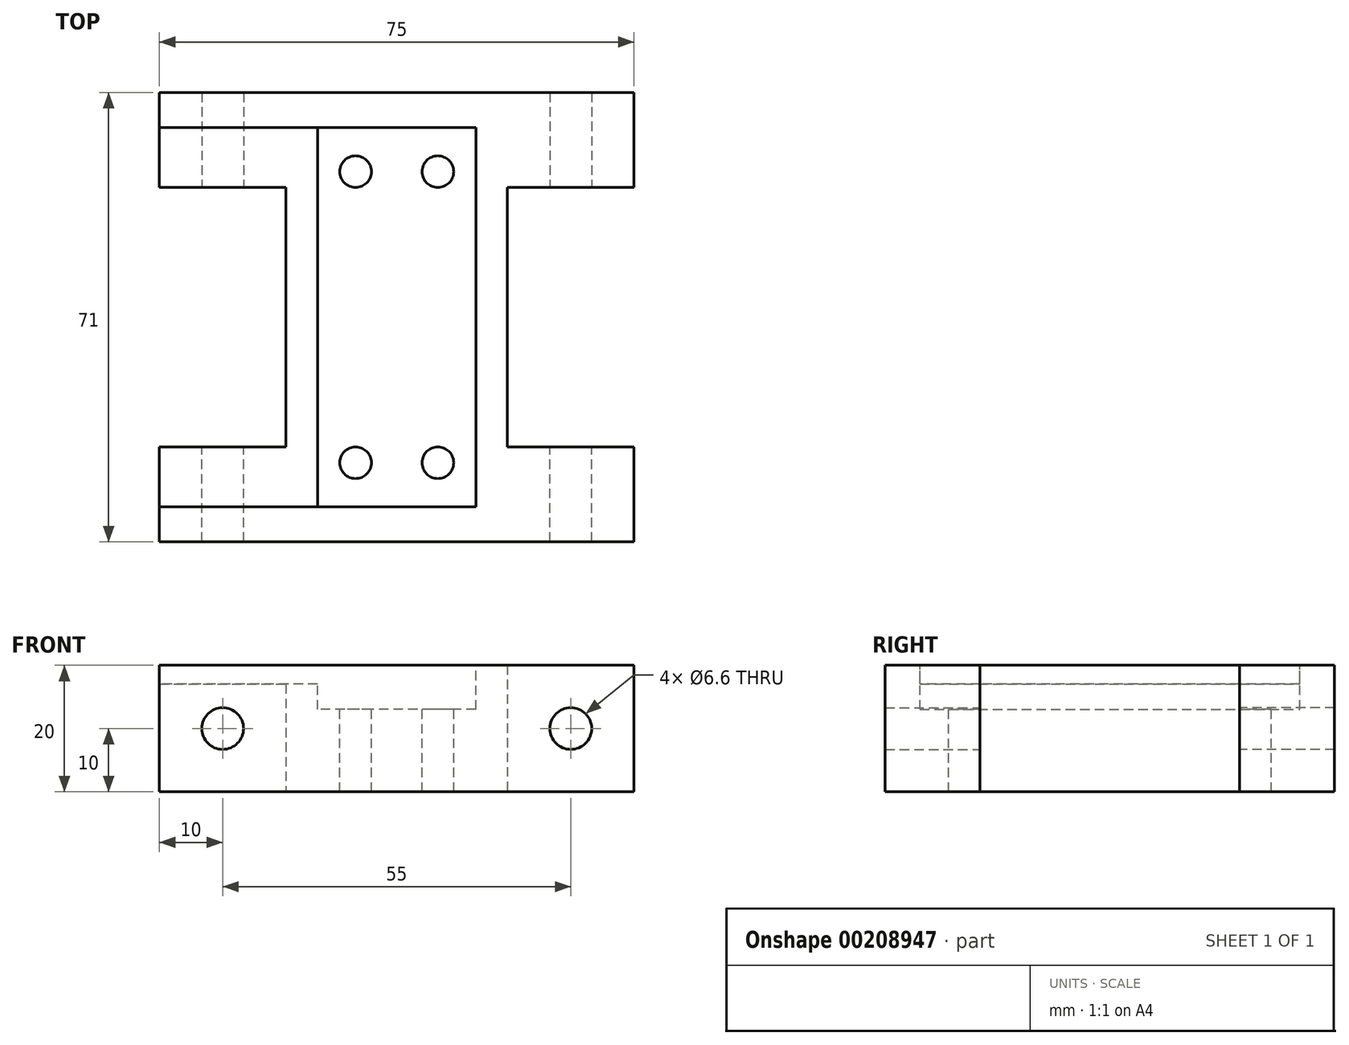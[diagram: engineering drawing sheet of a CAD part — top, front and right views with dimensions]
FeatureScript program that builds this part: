
annotation { "Feature Type Name" : "Feature", "Feature Type Description" : "" }
export const myFeature = defineFeature(function(context is Context, id is Id, definition is map)
    precondition{}
    {
        {
            var Q0;
            Q0=qCreatedBy(makeId("Top.planeOp"),FACE);
            var sketch = newSketch(context, id + "F0", { "sketchPlane" : qUnion([Q0])});
            skLineSegment(sketch, "E0.bottom", {"start": v(-37.5, 35.5) * mm, "end": v(37.5, 35.5) * mm});
            skLineSegment(sketch, "E0.top", {"start": v(-37.5, -35.5) * mm, "end": v(37.5, -35.5) * mm});
            skLineSegment(sketch, "E0.left", {"start": v(-37.5, 35.5) * mm, "end": v(-37.5, 20.5) * mm});
            skLineSegment(sketch, "E0.right", {"start": v(37.5, 35.5) * mm, "end": v(37.5, 20.5) * mm});
            skLineSegment(sketch, "E1", {"start": v(-37.5, 0) * mm, "end": v(37.5, 0) * mm, "construction": true});
            skPoint(sketch, "E1.endSnap0", {"position": v(37.5, 0) * mm});
            skLineSegment(sketch, "E2", {"start": v(0, 35.5) * mm, "end": v(0, -35.5) * mm, "construction": true});
            skLineSegment(sketch, "E3", {"start": v(-37.5, 20.5) * mm, "end": v(-17.5, 20.5) * mm});
            skLineSegment(sketch, "E4", {"start": v(-17.5, 20.5) * mm, "end": v(-17.5, 0) * mm});
            skLineSegment(sketch, "E5.MirrorCS", {"start": v(17.5, 20.5) * mm, "end": v(17.5, 0) * mm});
            skLineSegment(sketch, "E6.MirrorCS", {"start": v(37.5, 20.5) * mm, "end": v(17.5, 20.5) * mm});
            skLineSegment(sketch, "E7.MirrorCS", {"start": v(-17.5, -20.5) * mm, "end": v(-17.5, 0) * mm});
            skLineSegment(sketch, "E8.MirrorCS", {"start": v(17.5, -20.5) * mm, "end": v(17.5, 0) * mm});
            skLineSegment(sketch, "E9.MirrorCS", {"start": v(37.5, -20.5) * mm, "end": v(17.5, -20.5) * mm});
            skLineSegment(sketch, "E10.MirrorCS", {"start": v(-37.5, -20.5) * mm, "end": v(-17.5, -20.5) * mm});
            skLineSegment(sketch, "E11.trimOffspring", {"start": v(-37.5, -20.5) * mm, "end": v(-37.5, -35.5) * mm});
            skLineSegment(sketch, "E12.trimOffspring", {"start": v(37.5, -20.5) * mm, "end": v(37.5, -35.5) * mm});
            skPoint(sketch, "E13.orphan", {"position": v(41.38, 0) * mm});
            skSolve(sketch);
        }
        {
            var Q0;
            Q0=makeQuery(id+"F0.imprint","IMPRINT",FACE,{"disambiguationData":[TD([[makeQuery(id+"F0.imprint","IMPRINT",EDGE,{"derivedFrom":sQuery(id+"F0.wireOp",EDGE,"E0.bottom")}),-1.0]])]});
            extrude(context, id + "F1", {"entities" : qUnion([Q0]), "depth" : 20 * mm});
        }
        {
            var Q0;
            Q0=makeQuery(id+"F1.opExtrude","CAP_FACE",FACE,{"disambiguationData":[OSD([sQuery(id+"F0.wireOp",EDGE,"E0.bottom"),sQuery(id+"F0.wireOp",EDGE,"E0.top"),sQuery(id+"F0.wireOp",EDGE,"E0.left"),sQuery(id+"F0.wireOp",EDGE,"E0.right"),sQuery(id+"F0.wireOp",EDGE,"E3"),sQuery(id+"F0.wireOp",EDGE,"E4"),sQuery(id+"F0.wireOp",EDGE,"E5.MirrorCS"),sQuery(id+"F0.wireOp",EDGE,"E6.MirrorCS"),sQuery(id+"F0.wireOp",EDGE,"E7.MirrorCS"),sQuery(id+"F0.wireOp",EDGE,"E8.MirrorCS"),sQuery(id+"F0.wireOp",EDGE,"E9.MirrorCS"),sQuery(id+"F0.wireOp",EDGE,"E10.MirrorCS"),sQuery(id+"F0.wireOp",EDGE,"E11.trimOffspring"),sQuery(id+"F0.wireOp",EDGE,"E12.trimOffspring")])],"isStart":false});
            var sketch = newSketch(context, id + "F2", { "sketchPlane" : qUnion([Q0])});
            skLineSegment(sketch, "E14", {"start": v(0, 35.5) * mm, "end": v(0, -35.5) * mm, "construction": true});
            skLineSegment(sketch, "E15", {"start": v(-17.5, 0) * mm, "end": v(17.5, 0) * mm, "construction": true});
            skLineSegment(sketch, "E16.bottom", {"start": v(0, 0) * mm, "end": v(-12.5, 0) * mm});
            skLineSegment(sketch, "E16.top", {"start": v(0, 30) * mm, "end": v(-12.5, 30) * mm});
            skLineSegment(sketch, "E16.left", {"start": v(0, 0) * mm, "end": v(0, 30) * mm});
            skLineSegment(sketch, "E16.right", {"start": v(-12.5, 0) * mm, "end": v(-12.5, 30) * mm});
            skLineSegment(sketch, "E17.MirrorCS", {"start": v(12.5, 0) * mm, "end": v(12.5, 30) * mm});
            skLineSegment(sketch, "E18.MirrorCS", {"start": v(0, 30) * mm, "end": v(12.5, 30) * mm});
            skLineSegment(sketch, "E19.MirrorCS", {"start": v(0, -30) * mm, "end": v(12.5, -30) * mm});
            skLineSegment(sketch, "E20.MirrorCS", {"start": v(0, -30) * mm, "end": v(-12.5, -30) * mm});
            skLineSegment(sketch, "E21.MirrorCS", {"start": v(-12.5, 0) * mm, "end": v(-12.5, -30) * mm});
            skLineSegment(sketch, "E22.MirrorCS", {"start": v(12.5, 0) * mm, "end": v(12.5, -30) * mm});
            skLineSegment(sketch, "E23", {"start": v(-12.5, 30) * mm, "end": v(-37.5, 30) * mm});
            skLineSegment(sketch, "E24", {"start": v(-12.5, -30) * mm, "end": v(-37.5, -30) * mm});
            skSolve(sketch);
        }
        {
            var Q0;
            Q0=makeQuery(id+"F2.imprint","IMPRINT",FACE,{"disambiguationData":[TD([[makeQuery(id+"F2.imprint","IMPRINT",EDGE,{"derivedFrom":sQuery(id+"F2.wireOp",EDGE,"E16.bottom")}),-1.0]])]});
            var Q1;
            Q1=makeQuery(id+"F2.imprint","IMPRINT",FACE,{"disambiguationData":[TD([[makeQuery(id+"F2.imprint","IMPRINT",EDGE,{"derivedFrom":sQuery(id+"F2.wireOp",EDGE,"E16.bottom")}),1.0]])]});
            extrude(context, id + "F3", {"entities" : qUnion([Q0, Q1]), "operationType" : NewBodyOperationType.REMOVE, "oppositeDirection" : true, "depth" : 7 * mm});
        }
        {
            var Q0;
            Q0=makeQuery(id+"F2.imprint","IMPRINT",FACE,{"disambiguationData":[TD([[makeQuery(id+"F2.imprint","IMPRINT",EDGE,{"derivedFrom":sQuery(id+"F2.wireOp",EDGE,"E16.right")}),1.0]])]});
            extrude(context, id + "F4", {"entities" : qUnion([Q0]), "operationType" : NewBodyOperationType.REMOVE, "oppositeDirection" : true, "depth" : 3 * mm});
        }
        {
            var Q0;
            Q0=makeQuery(id+"F1.opExtrude","SWEPT_FACE",FACE,{"disambiguationData":[OSD([sQuery(id+"F0.wireOp",EDGE,"E6.MirrorCS")])]});
            var sketch = newSketch(context, id + "F5", { "sketchPlane" : qUnion([Q0])});
            skLineSegment(sketch, "E25", {"start": v(27.5, 20) * mm, "end": v(27.5, 0) * mm, "construction": true});
            skLineSegment(sketch, "E26", {"start": v(37.5, 10) * mm, "end": v(17.5, 10) * mm, "construction": true});
            skPoint(sketch, "E27", {"position": v(27.5, 10) * mm});
            skPoint(sketch, "E28.MirrorP", {"position": v(-27.5, 10) * mm});
            skSolve(sketch);
        }
        {
            var Q0;
            Q0=makeQuery(id+"F1.opExtrude","SWEPT_FACE",FACE,{"disambiguationData":[OSD([sQuery(id+"F0.wireOp",EDGE,"E9.MirrorCS")])]});
            var sketch = newSketch(context, id + "F6", { "sketchPlane" : qUnion([Q0])});
            skLineSegment(sketch, "E29", {"start": v(-27.5, 20) * mm, "end": v(-27.5, 0) * mm, "construction": true});
            skLineSegment(sketch, "E30", {"start": v(-17.5, 10) * mm, "end": v(-37.5, 10) * mm, "construction": true});
            skPoint(sketch, "E31", {"position": v(-27.5, 10) * mm});
            skPoint(sketch, "E32.MirrorP", {"position": v(27.5, 10) * mm});
            skSolve(sketch);
        }
        {
            var Q0;
            Q0=sQuery(id+"F6.wireOp",VERTEX,"E32.MirrorP");
            var Q1;
            Q1=sQuery(id+"F5.wireOp",VERTEX,"E28.MirrorP");
            var Q2;
            Q2=sQuery(id+"F5.wireOp",VERTEX,"E27");
            var Q3;
            Q3=sQuery(id+"F6.wireOp",VERTEX,"E31");
            var Q4;
            Q4=makeQuery(id+"F1.opExtrude","SWEPT_BODY",BODY,{"disambiguationData":[OSD([sQuery(id+"F0.wireOp",EDGE,"E0.bottom"),sQuery(id+"F0.wireOp",EDGE,"E0.top"),sQuery(id+"F0.wireOp",EDGE,"E0.left"),sQuery(id+"F0.wireOp",EDGE,"E0.right"),sQuery(id+"F0.wireOp",EDGE,"E3"),sQuery(id+"F0.wireOp",EDGE,"E4"),sQuery(id+"F0.wireOp",EDGE,"E5.MirrorCS"),sQuery(id+"F0.wireOp",EDGE,"E6.MirrorCS"),sQuery(id+"F0.wireOp",EDGE,"E7.MirrorCS"),sQuery(id+"F0.wireOp",EDGE,"E8.MirrorCS"),sQuery(id+"F0.wireOp",EDGE,"E9.MirrorCS"),sQuery(id+"F0.wireOp",EDGE,"E10.MirrorCS"),sQuery(id+"F0.wireOp",EDGE,"E11.trimOffspring"),sQuery(id+"F0.wireOp",EDGE,"E12.trimOffspring")])]});
            hole(context, id + "F7", {"style" : HoleStyle.SIMPLE, "endStyle" : HoleEndStyle.THROUGH, "standardTappedOrClearance" : lookupTablePath({ "standard" : "ISO", "fit" : "Normal", "size" : "M6", "type" : "Clearance" }), "standardBlindInLast" : lookupTablePath({ "fit" : "Standard", "standard" : "ISO", "size" : "M6", "type" : "Clearance" }), "holeDiameter" : 6.6 * mm, "locations" : qUnion([Q0, Q1, Q2, Q3]), "scope" : qUnion([Q4]), "isTappedThrough" : true});
        }
        {
            var Q0;
            Q0=makeQuery(id+"F2.imprint","IMPRINT",FACE,{"disambiguationData":[TD([[makeQuery(id+"F2.imprint","IMPRINT",EDGE,{"derivedFrom":sQuery(id+"F2.wireOp",EDGE,"E16.bottom")}),1.0]])]});
            var sketch = newSketch(context, id + "F8", { "sketchPlane" : qUnion([Q0])});
            skPoint(sketch, "E33", {"position": v(-6.5, 23) * mm});
            skPoint(sketch, "E34.MirrorP", {"position": v(-6.5, -23) * mm});
            skPoint(sketch, "E35.MirrorP", {"position": v(6.5, 23) * mm});
            skPoint(sketch, "E36.MirrorP", {"position": v(6.5, -23) * mm});
            skSolve(sketch);
        }
        {
            var Q0;
            Q0=sQuery(id+"F8.wireOp",VERTEX,"E33");
            var Q1;
            Q1=sQuery(id+"F8.wireOp",VERTEX,"E35.MirrorP");
            var Q2;
            Q2=sQuery(id+"F8.wireOp",VERTEX,"E36.MirrorP");
            var Q3;
            Q3=sQuery(id+"F8.wireOp",VERTEX,"E34.MirrorP");
            var Q4;
            Q4=makeQuery(id+"F1.opExtrude","SWEPT_BODY",BODY,{"disambiguationData":[OSD([sQuery(id+"F0.wireOp",EDGE,"E0.bottom"),sQuery(id+"F0.wireOp",EDGE,"E0.top"),sQuery(id+"F0.wireOp",EDGE,"E0.left"),sQuery(id+"F0.wireOp",EDGE,"E0.right"),sQuery(id+"F0.wireOp",EDGE,"E3"),sQuery(id+"F0.wireOp",EDGE,"E4"),sQuery(id+"F0.wireOp",EDGE,"E5.MirrorCS"),sQuery(id+"F0.wireOp",EDGE,"E6.MirrorCS"),sQuery(id+"F0.wireOp",EDGE,"E7.MirrorCS"),sQuery(id+"F0.wireOp",EDGE,"E8.MirrorCS"),sQuery(id+"F0.wireOp",EDGE,"E9.MirrorCS"),sQuery(id+"F0.wireOp",EDGE,"E10.MirrorCS"),sQuery(id+"F0.wireOp",EDGE,"E11.trimOffspring"),sQuery(id+"F0.wireOp",EDGE,"E12.trimOffspring")])]});
            hole(context, id + "F9", {"style" : HoleStyle.SIMPLE, "endStyle" : HoleEndStyle.THROUGH, "standardTappedOrClearance" : lookupTablePath({ "standard" : "ISO", "engagement" : "75%", "pitch" : "1 mm", "size" : "M6", "type" : "Tapped" }), "standardBlindInLast" : lookupTablePath({ "standard" : "ISO", "engagement" : "75%", "pitch" : "1 mm", "size" : "M6", "type" : "Tapped" }), "holeDiameter" : 5 * mm, "locations" : qUnion([Q0, Q1, Q2, Q3]), "scope" : qUnion([Q4]), "isTappedThrough" : true, "majorDiameter" : 6 * mm, "showTappedDepth" : true});
        }
    });
